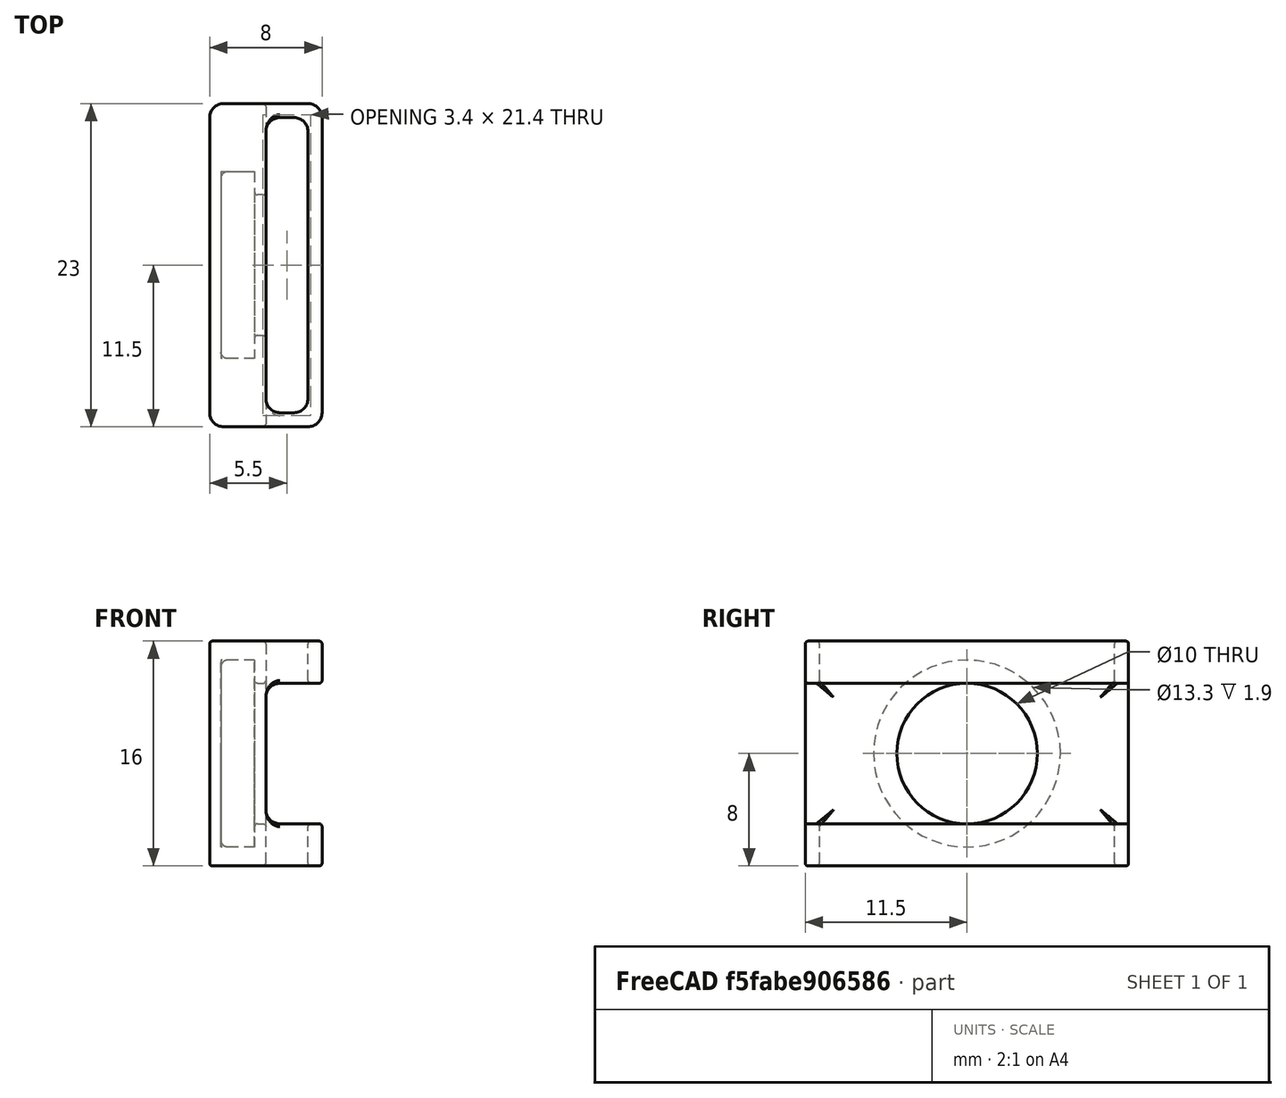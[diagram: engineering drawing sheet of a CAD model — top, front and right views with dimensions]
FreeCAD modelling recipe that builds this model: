
FCSTD DOCUMENT  (FreeCAD 1.0RUnknown)
Label: watch-band-rfid
License: All rights reserved
LicenseURL: https://en.wikipedia.org/wiki/All_rights_reserved
objects: PartDesign::Fillet×6, Sketcher::SketchObject×4, PartDesign::Pad×2, PartDesign::Pocket×2, PartDesign::Body×2, PartDesign::Plane×1, PartDesign::SubShapeBinder×1, PartDesign::Boolean×1
note: 44 computed .brp shape members not serialized (recipe doc carries the construction recipe); baked Part::Feature solids carry a one-line shape summary decoded from their .brp

FEATURE [Sketcher::SketchObject] Sketch
  ArcFitTolerance = 1e-06
  AttachmentSupport = -> [XY_Plane]
  FullyConstrained = false
  MakeInternals = false
  MapMode = 5
  sketch-geometry (10):
    g0: LineSegment StartX=0 StartY=11.5 StartZ=0 EndX=0 EndY=-11.5 EndZ=0
    g1: LineSegment StartX=0 StartY=11.5 StartZ=0 EndX=14.0939 EndY=11.5 EndZ=0
    g2: LineSegment StartX=14.0939 StartY=11.5 StartZ=0 EndX=8 EndY=11.5 EndZ=0
    g3: LineSegment StartX=8 StartY=11.5 StartZ=0 EndX=8 EndY=-11.5 EndZ=0
    g4: LineSegment StartX=0 StartY=-11.5 StartZ=0 EndX=8 EndY=-11.5 EndZ=0
    g5: LineSegment StartX=4 StartY=10.5 StartZ=0 EndX=4 EndY=-10.5 EndZ=0
    g6: LineSegment StartX=4 StartY=-10.5 StartZ=0 EndX=7 EndY=-10.5 EndZ=0
    g7: LineSegment StartX=7 StartY=-10.5 StartZ=0 EndX=7 EndY=10.5 EndZ=0
    g8: LineSegment StartX=7 StartY=10.5 StartZ=0 EndX=4 EndY=10.5 EndZ=0
    g9: LineSegment [constr] StartX=0 StartY=0 StartZ=0 EndX=8 EndY=-4e-16 EndZ=0
  constraints (26):
    c: PointOnObject(g0,g-2)
    c: Symmetric(g0,g0,g-1)
    c: Coincident(g1,g0)
    c: Horizontal(g1)
    c: Coincident(g2,g1)
    c: Horizontal(g2)
    c: Coincident(g3,g2)
    c: Vertical(g3)
    c: Coincident(g4,g0)
    c: Coincident(g4,g3)
    c: Horizontal(g4)
    c: Coincident(g5,g6)
    c: Coincident(g6,g7)
    c: Coincident(g7,g8)
    c: Coincident(g8,g5)
    c: Vertical(g7)
    c: Horizontal(g6)
    c: Horizontal(g8)
    c: DistanceY(g0,g0) = 23
    c: Distance(g6,g6) = 3
    c: Coincident(g9,g-1)
    c: Symmetric(g3,g3,g9)
    c: Symmetric(g5,g5,g9)
    c: Distance(g3,g7) = 1
    c: Distance(g2,g8) = 1
    c: Distance(g5,g0) = 4
FEATURE [PartDesign::Pad] Pad
  Direction = (0,0,1)
  Length = 16
  Length2 = 10
  Profile = -> Sketch
  ReferenceAxis = -> Sketch [N_Axis]
  Refine = true
  Suppressed = false
  Type = 0
FEATURE [Sketcher::SketchObject] Sketch001
  ArcFitTolerance = 1e-06
  AttachmentSupport = -> [Pad]
  ExternalGeometry = -> [Pad]
  FullyConstrained = true
  MakeInternals = false
  MapMode = 5
  Placement = pos=(8,0,0) rot=(0.57735,0.57735,0.57735;2.0944rad)
  sketch-geometry (8):
    g0: LineSegment [constr] StartX=-11.5 StartY=16 StartZ=0 EndX=11.5 EndY=0 EndZ=0
    g1: LineSegment [constr] StartX=11.5 StartY=16 StartZ=0 EndX=-11.5 EndY=0 EndZ=0
    g2: GeomPoint [constr] X=0 Y=8 Z=0
    g3: LineSegment StartX=-11.5 StartY=13 StartZ=0 EndX=-11.5 EndY=3 EndZ=0
    g4: LineSegment StartX=-11.5 StartY=3 StartZ=0 EndX=11.5 EndY=3 EndZ=0
    g5: LineSegment StartX=11.5 StartY=3 StartZ=0 EndX=11.5 EndY=13 EndZ=0
    g6: LineSegment StartX=11.5 StartY=13 StartZ=0 EndX=-11.5 EndY=13 EndZ=0
    g7: GeomPoint [constr] X=0 Y=8 Z=0
  constraints (17):
    c: Coincident(g0,g-4)
    c: Coincident(g0,g-6)
    c: Coincident(g1,g-5)
    c: Coincident(g1,g-6)
    c: Symmetric(g0,g0,g2)
    c: Coincident(g3,g4)
    c: Coincident(g4,g5)
    c: Coincident(g5,g6)
    c: Coincident(g6,g3)
    c: Vertical(g3)
    c: Vertical(g5)
    c: Horizontal(g4)
    c: Horizontal(g6)
    c: Symmetric(g5,g3,g7)
    c: Coincident(g7,g2)
    c: PointOnObject(g4,g-5)
    c: Distance(g5,g5) = 10
FEATURE [PartDesign::Pocket] Pocket
  BaseFeature = -> Pad
  Direction = (-1,0,0)
  Length = 4
  Length2 = 5
  Profile = -> Sketch001
  ReferenceAxis = -> Sketch001 [N_Axis]
  Refine = true
  Suppressed = false
  Type = 0
FEATURE [PartDesign::Plane] DatumPlane
  AttachmentOffset = pos=(0,0,2) rot=(0,0,1;0rad)
  AttachmentSupport = -> [YZ_Plane001]
  Length = 60
  MapMode = 5
  Placement = pos=(2,0,0) rot=(0.57735,0.57735,0.57735;2.0944rad)
  ResizeMode = 0
  Width = 60
FEATURE [PartDesign::SubShapeBinder] Binder
  BindCopyOnChange = 0
  BindMode = 0
  ClaimChildren = false
  Context = -> Body [Boolean.Body001.Binder.]
  Fuse = false
  MakeFace = true
  OffsetFill = false
  OffsetIntersection = false
  OffsetJoinType = 0
  OffsetOpenResult = false
  PartialLoad = false
  Refine = true
  Relative = true
  Support = -> [Body[Pocket.Face16]]
  _Version = 2
FEATURE [Sketcher::SketchObject] Sketch002
  ArcFitTolerance = 1e-06
  AttachmentSupport = -> [DatumPlane]
  ExternalGeometry = -> [Binder]
  FullyConstrained = true
  MakeInternals = false
  MapMode = 5
  Placement = pos=(2,0,0) rot=(0.57735,0.57735,0.57735;2.0944rad)
  sketch-geometry (5):
    g0: LineSegment [constr] StartX=-10.5 StartY=16 StartZ=0 EndX=10.5 EndY=1.8e-15 EndZ=0
    g1: LineSegment [constr] StartX=-10.5 StartY=0 StartZ=0 EndX=10.5 EndY=16 EndZ=0
    g2: GeomPoint [constr] X=0 Y=8 Z=0
    g3: Circle CenterX=0 CenterY=8 CenterZ=0 NormalX=0 NormalY=0 NormalZ=1 AngleXU=0 Radius=6.65
    g4: GeomPoint [constr] X=0 Y=8 Z=0
  constraints (9):
    c: Coincident(g0,g-3)
    c: PointOnObject(g0,g-4)
    c: Coincident(g1,g-4)
    c: Coincident(g1,g-3)
    c: PointOnObject(g2,g-2)
    c: Coincident(g3,g2)
    c: Diameter(g3) = 13.3
    c: Symmetric(g0,g0,g4)
    c: Coincident(g2,g4)
FEATURE [PartDesign::Pad] Pad001
  Direction = (1,0,0)
  Length = 1.2
  Length2 = 1.2
  Placement = pos=(2,0,0) rot=(0.57735,0.57735,0.57735;2.0944rad)
  Profile = -> Sketch002
  ReferenceAxis = -> Sketch002 [N_Axis]
  Refine = true
  Suppressed = false
  Type = 4
FEATURE [PartDesign::Body] Body001  label="Chip"
  AllowCompound = false
  Group = -> [DatumPlane,Binder,Sketch002,Pad001]
  Origin = -> Origin001
  Tip = -> Pad001
FEATURE [Sketcher::SketchObject] Sketch003
  ArcFitTolerance = 1e-06
  AttachmentSupport = -> [Pocket]
  ExternalGeometry = -> [Pocket]
  FullyConstrained = true
  MakeInternals = false
  MapMode = 5
  Placement = pos=(4,-1e-16,0) rot=(0.57735,0.57735,0.57735;2.0944rad)
  sketch-geometry (4):
    g0: LineSegment [constr] StartX=-11.5 StartY=16 StartZ=0 EndX=11.5 EndY=0 EndZ=0
    g1: LineSegment [constr] StartX=11.5 StartY=16 StartZ=0 EndX=-11.5 EndY=0 EndZ=0
    g2: GeomPoint [constr] X=0 Y=8 Z=0
    g3: Circle CenterX=0 CenterY=8 CenterZ=0 NormalX=0 NormalY=0 NormalZ=1 AngleXU=0 Radius=5
  constraints (7):
    c: Coincident(g0,g-3)
    c: Coincident(g0,g-4)
    c: Coincident(g1,g-3)
    c: Coincident(g1,g-4)
    c: Symmetric(g0,g0,g2)
    c: Coincident(g3,g2)
    c: Diameter(g3) = 10
FEATURE [PartDesign::Pocket] Pocket001
  BaseFeature = -> Pocket
  Direction = (-1,0,0)
  Length = 1.5
  Length2 = 5
  Profile = -> Sketch003
  ReferenceAxis = -> Sketch003 [N_Axis]
  Refine = true
  Suppressed = false
  Type = 0
FEATURE [PartDesign::Boolean] Boolean
  BaseFeature = -> Pocket001
  Group = -> [Body001]
  Refine = true
  Suppressed = false
  Type = 1
  UsePlacement = true
FEATURE [PartDesign::Fillet] Fillet
  Base = -> Boolean [Edge46,Edge2,Edge1,Edge37,Edge47,Edge36,Edge40,Edge5,Edge13,Edge17,Edge38,Edge9,Edge49,Edge48]
  BaseFeature = -> Boolean
  Radius = 1
  Refine = true
  SupportTransform = false
  Suppressed = false
  UseAllEdges = false
FEATURE [PartDesign::Fillet] Fillet001
  Base = -> Fillet [Face31]
  BaseFeature = -> Fillet
  Radius = 0.2
  Refine = true
  SupportTransform = false
  Suppressed = false
  UseAllEdges = false
FEATURE [PartDesign::Fillet] Fillet002
  Base = -> Fillet001 [Edge104]
  BaseFeature = -> Fillet001
  Radius = 0.5
  Refine = true
  SupportTransform = false
  Suppressed = false
  UseAllEdges = false
FEATURE [PartDesign::Fillet] Fillet003
  Base = -> Fillet002 [Edge82,Edge28,Edge29,Edge43]
  BaseFeature = -> Fillet002
  Radius = 0.2
  Refine = true
  SupportTransform = false
  Suppressed = false
  UseAllEdges = false
FEATURE [PartDesign::Fillet] Fillet004
  Base = -> Fillet003 [Edge8,Edge12,Edge9,Edge5]
  BaseFeature = -> Fillet003
  Radius = 1
  Refine = true
  SupportTransform = false
  Suppressed = false
  UseAllEdges = false
FEATURE [PartDesign::Fillet] Fillet005
  Base = -> Fillet004 [Edge55,Edge73,Edge58,Edge76]
  BaseFeature = -> Fillet004
  Radius = 0.2
  Refine = true
  SupportTransform = false
  Suppressed = false
  UseAllEdges = false
FEATURE [PartDesign::Body] Body  label="Band"
  AllowCompound = false
  Group = -> [Sketch,Pad,Sketch001,Pocket,Sketch003,Pocket001,Boolean,Fillet,Fillet001,Fillet002,Fillet003,Fillet004,Fillet005]
  Origin = -> Origin
  Tip = -> Fillet005
